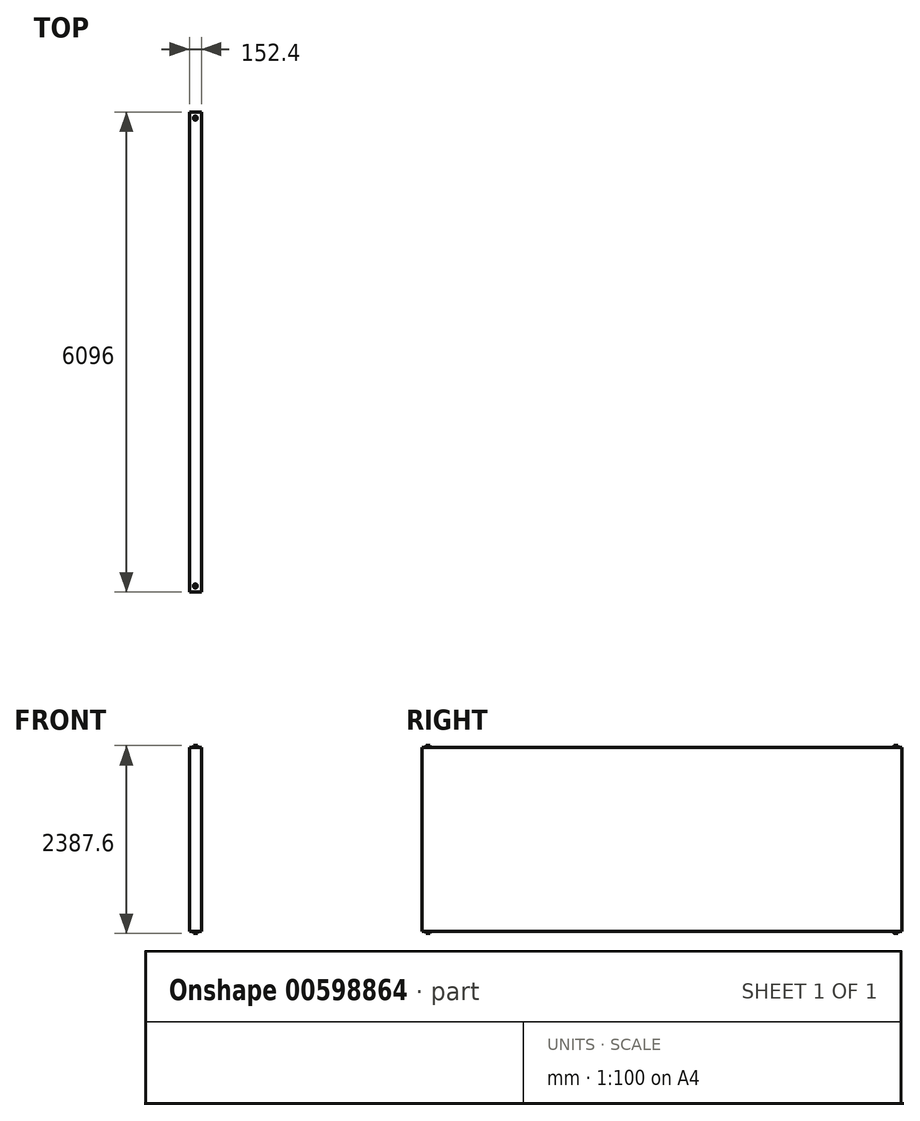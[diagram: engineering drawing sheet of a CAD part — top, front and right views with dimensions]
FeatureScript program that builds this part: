
annotation { "Feature Type Name" : "Feature", "Feature Type Description" : "" }
export const myFeature = defineFeature(function(context is Context, id is Id, definition is map)
    precondition{}
    {
        {
            var Q0;
            Q0=qCreatedBy(makeId("Top.planeOp"),FACE);
            var sketch = newSketch(context, id + "F0", { "sketchPlane" : qUnion([Q0])});
            skLineSegment(sketch, "E0.bottom", {"start": v(76.2, 3048) * mm, "end": v(-76.2, 3048) * mm});
            skLineSegment(sketch, "E0.top", {"start": v(76.2, -3048) * mm, "end": v(-76.2, -3048) * mm});
            skLineSegment(sketch, "E0.left", {"start": v(76.2, 3048) * mm, "end": v(76.2, -3048) * mm});
            skLineSegment(sketch, "E0.right", {"start": v(-76.2, 3048) * mm, "end": v(-76.2, -3048) * mm});
            skPoint(sketch, "E0.middle", {"position": v(0, 0) * mm});
            skSolve(sketch);
        }
        {
            var Q0;
            Q0=makeQuery(id+"F0.imprint","IMPRINT",FACE,{"disambiguationData":[TD([[makeQuery(id+"F0.imprint","IMPRINT",EDGE,{"derivedFrom":sQuery(id+"F0.wireOp",EDGE,"E0.bottom")}),1.0]])]});
            extrude(context, id + "F1", {"entities" : qUnion([Q0]), "depth" : 2336.8 * mm, "offsetDistance" : 25.4 * mm});
        }
        {
            var Q0;
            Q0=makeQuery(id+"F1.opExtrude","CAP_FACE",FACE,{"disambiguationData":[OSD([sQuery(id+"F0.wireOp",EDGE,"E0.bottom"),sQuery(id+"F0.wireOp",EDGE,"E0.top"),sQuery(id+"F0.wireOp",EDGE,"E0.left"),sQuery(id+"F0.wireOp",EDGE,"E0.right")])],"isStart":false});
            var sketch = newSketch(context, id + "F2", { "sketchPlane" : qUnion([Q0])});
            skLineSegment(sketch, "E1.bottom", {"start": v(76.2, -3048) * mm, "end": v(0, -3048) * mm});
            skLineSegment(sketch, "E1.top", {"start": v(76.2, -2971.8) * mm, "end": v(0, -2971.8) * mm});
            skLineSegment(sketch, "E1.left", {"start": v(76.2, -3048) * mm, "end": v(76.2, -2971.8) * mm});
            skLineSegment(sketch, "E1.right", {"start": v(0, -3048) * mm, "end": v(0, -2971.8) * mm});
            skCircle(sketch, "E2", {"center": v(0, -2971.8) * mm, "radius": 25.4 * mm});
            skLineSegment(sketch, "E3.bottom", {"start": v(76.2, 3048) * mm, "end": v(0, 3048) * mm});
            skLineSegment(sketch, "E3.top", {"start": v(76.2, 2971.8) * mm, "end": v(0, 2971.8) * mm});
            skLineSegment(sketch, "E3.left", {"start": v(76.2, 3048) * mm, "end": v(76.2, 2971.8) * mm});
            skLineSegment(sketch, "E3.right", {"start": v(0, 3048) * mm, "end": v(0, 2971.8) * mm});
            skCircle(sketch, "E4", {"center": v(0, 2971.8) * mm, "radius": 25.4 * mm});
            skSolve(sketch);
        }
        {
            var Q0;
            {var subQ0=sQuery(id+"F2.wireOp",EDGE,"E3.right");var subQ1=sQuery(id+"F2.wireOp",EDGE,"E3.top");var subQ2=makeQuery(id+"F2.imprint","INTERSECT",VERTEX,{"derivedFrom":[subQ1,subQ0]});Q0=makeQuery(id+"F2.imprint","IMPRINT",FACE,{"disambiguationData":[TD([[makeQuery(id+"F2.imprint","IMPRINT",EDGE,{"disambiguationData":[TD([[subQ2,1.0]])],"derivedFrom":subQ1}),-1.0]])]});}
            var Q1;
            {var subQ0=sQuery(id+"F2.wireOp",EDGE,"E3.right");var subQ1=sQuery(id+"F2.wireOp",EDGE,"E3.top");var subQ2=makeQuery(id+"F2.imprint","INTERSECT",VERTEX,{"derivedFrom":[subQ1,subQ0]});Q1=makeQuery(id+"F2.imprint","IMPRINT",FACE,{"disambiguationData":[TD([[makeQuery(id+"F2.imprint","IMPRINT",EDGE,{"disambiguationData":[TD([[subQ2,1.0]])],"derivedFrom":subQ1}),1.0]])]});}
            var Q2;
            {var subQ0=sQuery(id+"F2.wireOp",EDGE,"E1.right");var subQ1=sQuery(id+"F2.wireOp",EDGE,"E1.top");var subQ2=makeQuery(id+"F2.imprint","INTERSECT",VERTEX,{"derivedFrom":[subQ1,subQ0]});Q2=makeQuery(id+"F2.imprint","IMPRINT",FACE,{"disambiguationData":[TD([[makeQuery(id+"F2.imprint","IMPRINT",EDGE,{"disambiguationData":[TD([[subQ2,1.0]])],"derivedFrom":subQ1}),-1.0]])]});}
            var Q3;
            {var subQ0=sQuery(id+"F2.wireOp",EDGE,"E1.right");var subQ1=sQuery(id+"F2.wireOp",EDGE,"E1.top");var subQ2=makeQuery(id+"F2.imprint","INTERSECT",VERTEX,{"derivedFrom":[subQ1,subQ0]});Q3=makeQuery(id+"F2.imprint","IMPRINT",FACE,{"disambiguationData":[TD([[makeQuery(id+"F2.imprint","IMPRINT",EDGE,{"disambiguationData":[TD([[subQ2,1.0]])],"derivedFrom":subQ1}),1.0]])]});}
            extrude(context, id + "F3", {"entities" : qUnion([Q0, Q1, Q2, Q3]), "operationType" : NewBodyOperationType.ADD, "depth" : 25.4 * mm, "offsetDistance" : 25.4 * mm});
        }
        {
            var Q0;
            Q0=makeQuery(id+"F1.opExtrude","CAP_FACE",FACE,{"disambiguationData":[OSD([sQuery(id+"F0.wireOp",EDGE,"E0.bottom"),sQuery(id+"F0.wireOp",EDGE,"E0.top"),sQuery(id+"F0.wireOp",EDGE,"E0.left"),sQuery(id+"F0.wireOp",EDGE,"E0.right")])],"isStart":true});
            var sketch = newSketch(context, id + "F4", { "sketchPlane" : qUnion([Q0])});
            skLineSegment(sketch, "E5.bottom", {"start": v(76.2, 3048) * mm, "end": v(0, 3048) * mm});
            skLineSegment(sketch, "E5.top", {"start": v(76.2, 2971.8) * mm, "end": v(0, 2971.8) * mm});
            skLineSegment(sketch, "E5.left", {"start": v(76.2, 3048) * mm, "end": v(76.2, 2971.8) * mm});
            skLineSegment(sketch, "E5.right", {"start": v(0, 3048) * mm, "end": v(0, 2971.8) * mm});
            skCircle(sketch, "E6", {"center": v(0, 2971.8) * mm, "radius": 25.4 * mm});
            skLineSegment(sketch, "E7.bottom", {"start": v(76.2, -3048) * mm, "end": v(0, -3048) * mm});
            skLineSegment(sketch, "E7.top", {"start": v(76.2, -2971.8) * mm, "end": v(0, -2971.8) * mm});
            skLineSegment(sketch, "E7.left", {"start": v(76.2, -3048) * mm, "end": v(76.2, -2971.8) * mm});
            skLineSegment(sketch, "E7.right", {"start": v(0, -3048) * mm, "end": v(0, -2971.8) * mm});
            skCircle(sketch, "E8", {"center": v(0, -2971.8) * mm, "radius": 25.4 * mm});
            skSolve(sketch);
        }
        {
            var Q0;
            {var subQ0=sQuery(id+"F4.wireOp",EDGE,"E5.right");var subQ1=sQuery(id+"F4.wireOp",EDGE,"E5.top");var subQ2=makeQuery(id+"F4.imprint","INTERSECT",VERTEX,{"derivedFrom":[subQ1,subQ0]});Q0=makeQuery(id+"F4.imprint","IMPRINT",FACE,{"disambiguationData":[TD([[makeQuery(id+"F4.imprint","IMPRINT",EDGE,{"disambiguationData":[TD([[subQ2,1.0]])],"derivedFrom":subQ1}),-1.0]])]});}
            var Q1;
            {var subQ0=sQuery(id+"F4.wireOp",EDGE,"E5.right");var subQ1=sQuery(id+"F4.wireOp",EDGE,"E5.top");var subQ2=makeQuery(id+"F4.imprint","INTERSECT",VERTEX,{"derivedFrom":[subQ1,subQ0]});Q1=makeQuery(id+"F4.imprint","IMPRINT",FACE,{"disambiguationData":[TD([[makeQuery(id+"F4.imprint","IMPRINT",EDGE,{"disambiguationData":[TD([[subQ2,1.0]])],"derivedFrom":subQ1}),1.0]])]});}
            var Q2;
            {var subQ0=sQuery(id+"F4.wireOp",EDGE,"E7.right");var subQ1=sQuery(id+"F4.wireOp",EDGE,"E7.top");var subQ2=makeQuery(id+"F4.imprint","INTERSECT",VERTEX,{"derivedFrom":[subQ1,subQ0]});Q2=makeQuery(id+"F4.imprint","IMPRINT",FACE,{"disambiguationData":[TD([[makeQuery(id+"F4.imprint","IMPRINT",EDGE,{"disambiguationData":[TD([[subQ2,1.0]])],"derivedFrom":subQ1}),1.0]])]});}
            var Q3;
            {var subQ0=sQuery(id+"F4.wireOp",EDGE,"E7.right");var subQ1=sQuery(id+"F4.wireOp",EDGE,"E7.top");var subQ2=makeQuery(id+"F4.imprint","INTERSECT",VERTEX,{"derivedFrom":[subQ1,subQ0]});Q3=makeQuery(id+"F4.imprint","IMPRINT",FACE,{"disambiguationData":[TD([[makeQuery(id+"F4.imprint","IMPRINT",EDGE,{"disambiguationData":[TD([[subQ2,1.0]])],"derivedFrom":subQ1}),-1.0]])]});}
            extrude(context, id + "F5", {"entities" : qUnion([Q0, Q1, Q2, Q3]), "operationType" : NewBodyOperationType.ADD, "depth" : 25.4 * mm, "offsetDistance" : 25.4 * mm});
        }
    });
